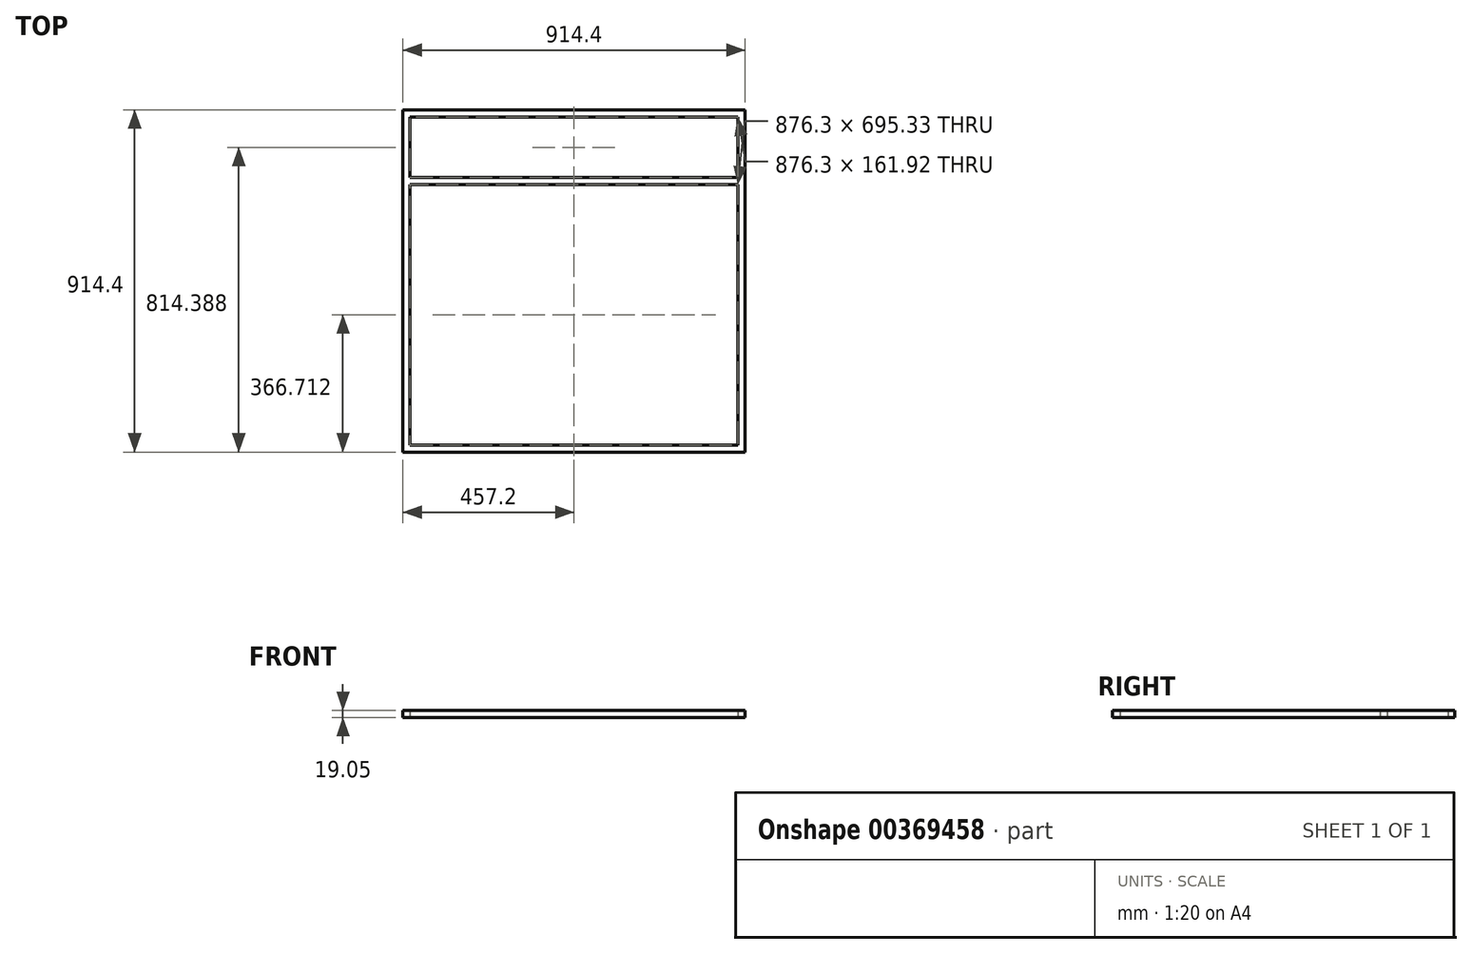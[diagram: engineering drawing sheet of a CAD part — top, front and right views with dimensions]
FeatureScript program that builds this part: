
annotation { "Feature Type Name" : "Feature", "Feature Type Description" : "" }
export const myFeature = defineFeature(function(context is Context, id is Id, definition is map)
    precondition{}
    {
        {
            var Q0;
            Q0=qCreatedBy(makeId("Top.planeOp"),FACE);
            var sketch = newSketch(context, id + "F0", { "sketchPlane" : qUnion([Q0])});
            skLineSegment(sketch, "E0.bottom", {"start": v(438.15, 438.15) * mm, "end": v(-438.15, 438.15) * mm});
            skLineSegment(sketch, "E0.top", {"start": v(438.15, -438.15) * mm, "end": v(-438.15, -438.15) * mm});
            skLineSegment(sketch, "E0.left", {"start": v(438.15, 438.15) * mm, "end": v(438.15, -438.15) * mm});
            skLineSegment(sketch, "E0.right", {"start": v(-438.15, 438.15) * mm, "end": v(-438.15, -438.15) * mm});
            skPoint(sketch, "E0.middle", {"position": v(0, 0) * mm});
            skLineSegment(sketch, "E1.bottom", {"start": v(457.2, 457.2) * mm, "end": v(-457.2, 457.2) * mm});
            skLineSegment(sketch, "E1.top", {"start": v(457.2, -457.2) * mm, "end": v(-457.2, -457.2) * mm});
            skLineSegment(sketch, "E1.left", {"start": v(457.2, 457.2) * mm, "end": v(457.2, -457.2) * mm});
            skLineSegment(sketch, "E1.right", {"start": v(-457.2, 457.2) * mm, "end": v(-457.2, -457.2) * mm});
            skSolve(sketch);
        }
        {
            var Q0;
            Q0 = qSketchRegion(id + "F0", true);
            extrude(context, id + "F1", {"entities" : qUnion([Q0]), "depth" : 19.05 * mm});
        }
        {
            var Q0;
            Q0=qCreatedBy(makeId("Top.planeOp"),FACE);
            var sketch = newSketch(context, id + "F2", { "sketchPlane" : qUnion([Q0])});
            skLineSegment(sketch, "E2", {"start": v(0, 0) * mm, "end": v(0, 266.7) * mm});
            skLineSegment(sketch, "E3.bottom", {"start": v(438.15, 276.23) * mm, "end": v(-438.15, 276.23) * mm});
            skLineSegment(sketch, "E3.top", {"start": v(438.15, 257.18) * mm, "end": v(-438.15, 257.18) * mm});
            skLineSegment(sketch, "E3.left", {"start": v(438.15, 276.23) * mm, "end": v(438.15, 257.18) * mm});
            skLineSegment(sketch, "E3.right", {"start": v(-438.15, 276.23) * mm, "end": v(-438.15, 257.17) * mm});
            skPoint(sketch, "E3.middle", {"position": v(0, 266.7) * mm});
            skSolve(sketch);
        }
        {
            var Q0;
            Q0 = qSketchRegion(id + "F2", true);
            extrude(context, id + "F3", {"entities" : qUnion([Q0]), "operationType" : NewBodyOperationType.ADD, "depth" : 19.05 * mm});
        }
    });
